# Revit family: Wall Panel 1
name_source: partatom
category: Panneaux de murs-rideaux
revit_build: Autodesk Revit Architecture 2014 (Build: 20130308_1515(x64)
units: mm (PartAtom-declared; Revit-internal decimal feet)

## types (1)
- Wall Panel 1
    AT.Bamboo H façade haut hauteur = 300 mm  [stored 0.984252 ft]
    AT.Chanfrein H = 2000 mm  [stored 6.56168 ft]
    AT.Chanfrein V = 225 mm  [stored 0.738189 ft]
    AT.Décalage début tasseau 2 = 400 mm  [stored 1.31234 ft]
    AT.Décalage intérieur = 3000 mm  [stored 9.84252 ft]
    AT.Hauteur attique = 3500 mm
    AT.Longueur champ tasseau 2 = 4800 mm
    AT.Longueur poutre = 5600 mm  [stored 18.3727 ft]
    AT.Longueur tasseau 1 = 6200 mm  [stored 20.3412 ft]
    AT.Poteau extension haut = 1000 mm  [stored 3.28084 ft]
    AT.Poteau haut = 250 mm  [stored 0.82021 ft]
    AT.Poteaux décalage = 1100 mm
    AT.Poutre saillie = 1500 mm  [stored 4.92126 ft]
    AT.Séparation poteaux = 245 mm  [stored 0.803806 ft]
    AT.Séparation tasseaux 1 = 100 mm  [stored 0.328084 ft]
    AT.Séparation tasseaux 2 = 500 mm  [stored 1.64042 ft]
    AT.Tasseau Saillie = 600 mm
    AT.Tasseau largeur 1 = 50 mm  [stored 0.164042 ft]
    AT.Tasseau largeur 2 = 100 mm  [stored 0.328084 ft]
    AT.Tasseau profondeur 1 = 50 mm  [stored 0.164042 ft]
    AT.Tasseau profondeur 2 = 100 mm  [stored 0.328084 ft]
    Bamboo H Gap = 200 mm  [stored 0.656168 ft]
    Bamboo H Gap 0.5 = 100 mm  [stored 0.328084 ft]
    Bamboo H Offset = 150 mm
    Bamboo H façade bas hauteur = 0 mm  [stored 0 ft]
    Bamboo H façade haut hauteur = 0 mm  [stored 0 ft]
    Bamboo Matériau = <Par catégorie>
    Bamboo V Offset = 140 mm
    Bamboo V Separation = 600 mm
    Bamboo V2 Visibilité = Oui
    Bamboo diameter H = 60 mm  [stored 0.19685 ft]
    Bamboo diameter V = 60 mm  [stored 0.19685 ft]
    Bamboo radius H = 30 mm  [stored 0.0984252 ft]
    Bamboo radius V = 30 mm  [stored 0.0984252 ft]
    Cadre Matériau = <Par catégorie>
    Cadre remplissage largeur = 50 mm  [stored 0.164042 ft]
    Cadre remplissage profondeur = 30 mm  [stored 0.0984252 ft]
    Double Skin Offset = 300 mm  [stored 0.984252 ft]
    Frame Depth = 40 mm
    Frame Thickness = 75 mm
    Frame Thickness 0.5 = 38 mm
    Hauteur P2 = 1838 mm
    Hauteur P3 = 838 mm
    Head Height = 3000 mm  [stored 9.84252 ft]
    Infill Offset = 19 mm
    Marquise . Angle structure = 60.00°
    Marquise . Décalage Réseau Tasseaux 2 = 300 mm  [stored 0.984252 ft]
    Marquise . Décalage structure = 2500 mm  [stored 8.2021 ft]
    Marquise . Hauteur = 300 mm  [stored 0.984252 ft]
    Marquise . Hauteur Tasseaux 1 = 50 mm  [stored 0.164042 ft]
    Marquise . Hauteur Tasseaux 2 = 100 mm  [stored 0.328084 ft]
    Marquise . Hauteur poutres = 200 mm  [stored 0.656168 ft]
    Marquise . Séparation Tasseaux 1 = 100 mm  [stored 0.328084 ft]
    Marquise . Séparation Tasseaux 2 = 500 mm  [stored 1.64042 ft]
    Remplissage Matériau = <Par catégorie>
    Remplissage finition profondeur = 20 mm  [stored 0.0656168 ft]
    SOCLE.Bamboo H façade bas hauteur = 300 mm  [stored 0.984252 ft]
    SOCLE.Poteau extension bas = 600 mm
    Sill Height = 1200 mm
    Wall Gap H = 500 mm  [stored 1.64042 ft]
    Wall Gap H 0.5 = 250 mm  [stored 0.82021 ft]
    Wall Gap V = 200 mm  [stored 0.656168 ft]
    Wall Gap V 0.5 = 100 mm  [stored 0.328084 ft]

note: [stored X ft] marks values corroborated as IEEE doubles in the binary element streams (Revit-internal decimal feet)
